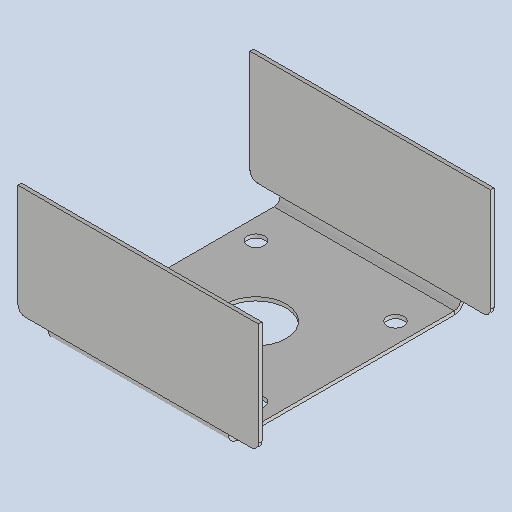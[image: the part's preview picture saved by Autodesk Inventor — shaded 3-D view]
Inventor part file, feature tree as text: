
AUTODESK INVENTOR PART (.ipt)
format: ipt  version: 2025 (Build 290162010, 162A)  size: 349,184 bytes
history: native  units: mm
features: sheet_metal_op x4, sketch x4, other x4, extrude x1, mirror x1, chamfer x1, projected_geometry x1
ambient origin geometry x8: Origin, YZ Plane, XZ Plane, XY Plane, X Axis, Y Axis, Z Axis, Center Point
bodies: Solid1 (feature_tree)
feature tree (16):
  sheet_metal_op  "Face1"
  sheet_metal_op  "Flange2"
  extrude  "Extrusion4"  Depth=3.0mm
  mirror  "Mirror1"
  chamfer  "Corner Round1"
  sketch  "Sketch1"  dims[d2=3.0mm d25=150.0mm]
  other  "Plate1"
  sketch  "Sketch5"  dims[d26=180.0mm]
  other  "Plate3"
  sheet_metal_op  "Bend2"
  sheet_metal_op  "Corner2"
  sketch  "Sketch6"  dims[d27=3.0mm]
  sketch  "Sketch10"  dims[d28=1.5mm d29=6.0mm d30=5.0mm d31=100.0mm d32=90.0deg d33=5.0mm d34=12.0mm d35=1.0mm d36=5.0mm d39=3.0mm d40=0.0mm d55=14.0mm d56=116.0mm d57=116.0mm d60=50.0mm d61=200.0mm d62=13.0mm d63=25.0mm d64=15.0mm d65=15.0mm d66=0.0mm d67=0.0mm d68=6.0mm]
  projected_geometry  "Projected Loop3"
  other  "Cut1"
  other  "Definition1"
